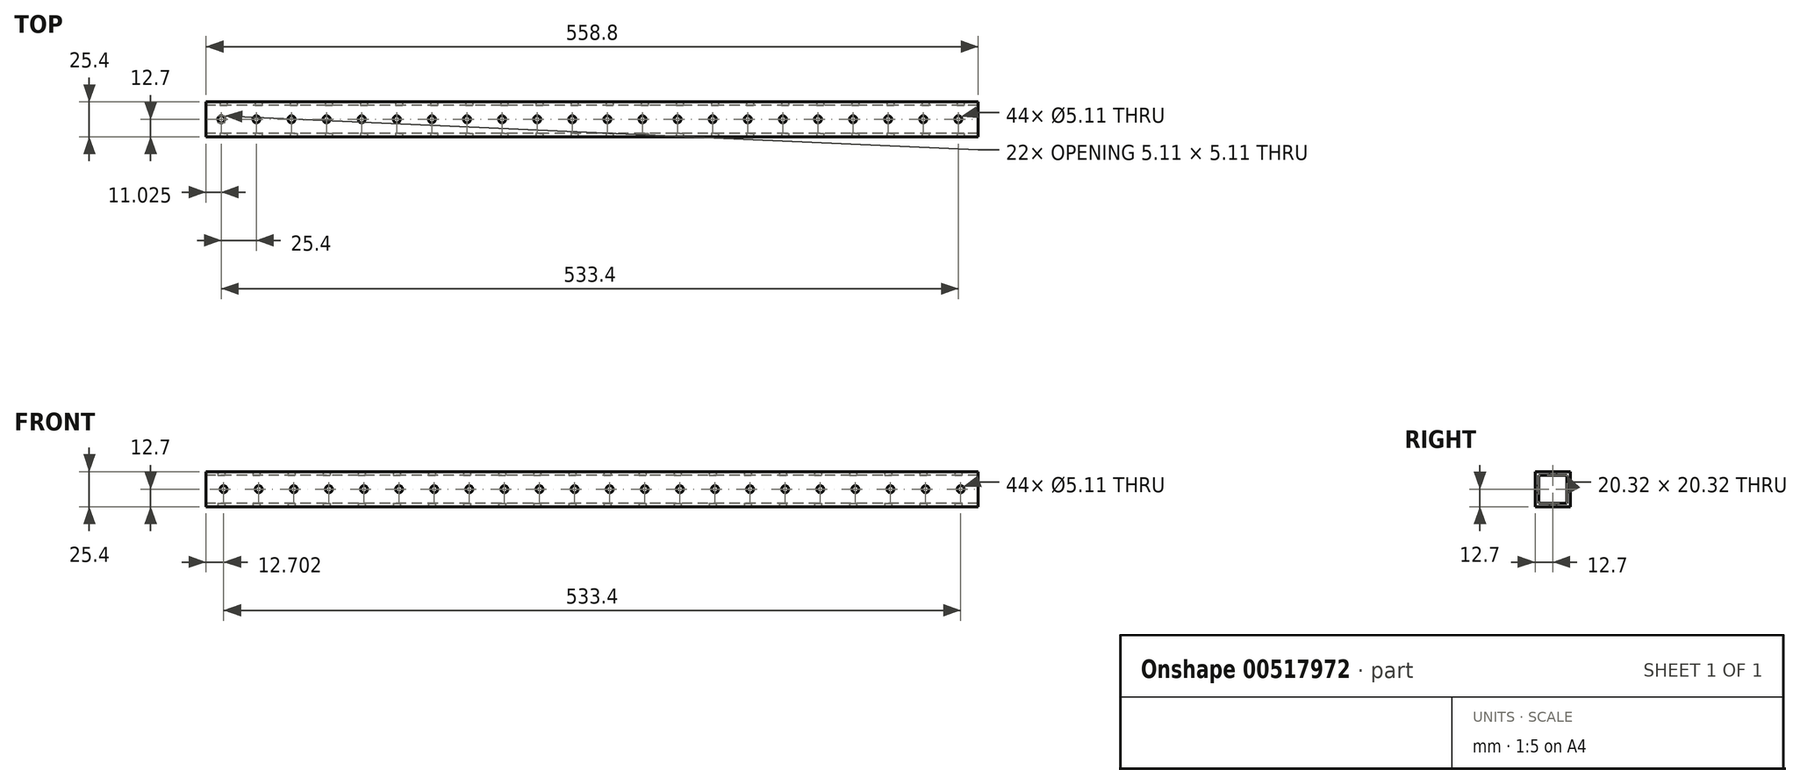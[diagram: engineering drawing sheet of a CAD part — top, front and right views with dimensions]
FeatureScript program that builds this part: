
annotation { "Feature Type Name" : "Feature", "Feature Type Description" : "" }
export const myFeature = defineFeature(function(context is Context, id is Id, definition is map)
    precondition{}
    {
        {
            var Q0;
            Q0=qCreatedBy(makeId("Top.planeOp"),FACE);
            var sketch = newSketch(context, id + "F0", { "sketchPlane" : qUnion([Q0])});
            skLineSegment(sketch, "E0.bottom", {"start": v(-249.34, 12.7) * mm, "end": v(309.46, 12.7) * mm});
            skLineSegment(sketch, "E0.top", {"start": v(-249.34, -12.7) * mm, "end": v(309.46, -12.7) * mm});
            skLineSegment(sketch, "E0.left", {"start": v(-249.34, 12.7) * mm, "end": v(-249.34, -12.7) * mm});
            skLineSegment(sketch, "E0.right", {"start": v(309.46, 12.7) * mm, "end": v(309.46, -12.7) * mm});
            skCircle(sketch, "E1", {"center": v(295.09, 0) * mm, "radius": 2.55 * mm});
            skCircle(sketch, "E2.1.0.0", {"center": v(269.69, 0) * mm, "radius": 2.55 * mm});
            skCircle(sketch, "E2.2.0.0", {"center": v(244.29, 0) * mm, "radius": 2.55 * mm});
            skCircle(sketch, "E2.3.0.0", {"center": v(218.89, 0) * mm, "radius": 2.55 * mm});
            skCircle(sketch, "E2.4.0.0", {"center": v(193.49, 0) * mm, "radius": 2.55 * mm});
            skCircle(sketch, "E2.5.0.0", {"center": v(168.09, 0) * mm, "radius": 2.55 * mm});
            skCircle(sketch, "E2.6.0.0", {"center": v(142.69, 0) * mm, "radius": 2.55 * mm});
            skCircle(sketch, "E2.7.0.0", {"center": v(117.29, 0) * mm, "radius": 2.55 * mm});
            skCircle(sketch, "E2.8.0.0", {"center": v(91.89, 0) * mm, "radius": 2.55 * mm});
            skCircle(sketch, "E2.9.0.0", {"center": v(66.49, 0) * mm, "radius": 2.55 * mm});
            skCircle(sketch, "E2.10.0.0", {"center": v(41.09, 0) * mm, "radius": 2.55 * mm});
            skCircle(sketch, "E2.11.0.0", {"center": v(15.69, 0) * mm, "radius": 2.55 * mm});
            skCircle(sketch, "E2.12.0.0", {"center": v(-9.71, 0) * mm, "radius": 2.55 * mm});
            skCircle(sketch, "E2.13.0.0", {"center": v(-35.11, 0) * mm, "radius": 2.55 * mm});
            skCircle(sketch, "E2.14.0.0", {"center": v(-60.51, 0) * mm, "radius": 2.55 * mm});
            skCircle(sketch, "E2.15.0.0", {"center": v(-85.91, 0) * mm, "radius": 2.55 * mm});
            skCircle(sketch, "E2.16.0.0", {"center": v(-111.31, 0) * mm, "radius": 2.55 * mm});
            skCircle(sketch, "E2.17.0.0", {"center": v(-136.71, 0) * mm, "radius": 2.55 * mm});
            skCircle(sketch, "E2.18.0.0", {"center": v(-162.11, 0) * mm, "radius": 2.55 * mm});
            skCircle(sketch, "E2.19.0.0", {"center": v(-187.51, 0) * mm, "radius": 2.55 * mm});
            skLineSegment(sketch, "E2.direction1", {"start": v(295.09, 0) * mm, "end": v(269.69, 0) * mm, "construction": true});
            skCircle(sketch, "E3.0.20.0", {"center": v(-212.91, 0) * mm, "radius": 2.55 * mm});
            skCircle(sketch, "E3.0.21.0", {"center": v(-238.31, 0) * mm, "radius": 2.55 * mm});
            skSolve(sketch);
        }
        {
            var Q0;
            Q0 = qSketchRegion(id + "F0", true);
            extrude(context, id + "F1", {"entities" : qUnion([Q0]), "depth" : 25.4 * mm, "offsetDistance" : 25.4 * mm});
        }
        {
            var Q0;
            Q0=makeQuery(id+"F1.opExtrude","SWEPT_FACE",FACE,{"disambiguationData":[OSD([sQuery(id+"F0.wireOp",EDGE,"E0.left")])]});
            var sketch = newSketch(context, id + "F2", { "sketchPlane" : qUnion([Q0])});
            skLineSegment(sketch, "E4.bottom", {"start": v(-10.16, 22.86) * mm, "end": v(10.16, 22.86) * mm});
            skLineSegment(sketch, "E4.top", {"start": v(-10.16, 2.54) * mm, "end": v(10.16, 2.54) * mm});
            skLineSegment(sketch, "E4.left", {"start": v(-10.16, 22.86) * mm, "end": v(-10.16, 2.54) * mm});
            skLineSegment(sketch, "E4.right", {"start": v(10.16, 22.86) * mm, "end": v(10.16, 2.54) * mm});
            skSolve(sketch);
        }
        {
            var Q0;
            Q0=makeQuery(id+"F2.imprint","IMPRINT",FACE,{"disambiguationData":[TD([[makeQuery(id+"F2.imprint","IMPRINT",EDGE,{"derivedFrom":sQuery(id+"F2.wireOp",EDGE,"E4.bottom")}),-1.0]])]});
            extrude(context, id + "F3", {"entities" : qUnion([Q0]), "operationType" : NewBodyOperationType.REMOVE, "oppositeDirection" : true, "depth" : 508 * mm, "offsetDistance" : 25.4 * mm});
        }
        {
            var Q0;
            Q0=makeQuery(id+"F1.opExtrude","SWEPT_FACE",FACE,{"disambiguationData":[OSD([sQuery(id+"F0.wireOp",EDGE,"E0.top")])]});
            var sketch = newSketch(context, id + "F4", { "sketchPlane" : qUnion([Q0])});
            skCircle(sketch, "E5", {"center": v(-236.64, 12.7) * mm, "radius": 2.55 * mm});
            skCircle(sketch, "E6.1.0.0", {"center": v(-211.24, 12.7) * mm, "radius": 2.55 * mm});
            skCircle(sketch, "E6.2.0.0", {"center": v(-185.84, 12.7) * mm, "radius": 2.55 * mm});
            skCircle(sketch, "E6.3.0.0", {"center": v(-160.44, 12.7) * mm, "radius": 2.55 * mm});
            skCircle(sketch, "E6.4.0.0", {"center": v(-135.04, 12.7) * mm, "radius": 2.55 * mm});
            skCircle(sketch, "E6.5.0.0", {"center": v(-109.64, 12.7) * mm, "radius": 2.55 * mm});
            skCircle(sketch, "E6.6.0.0", {"center": v(-84.24, 12.7) * mm, "radius": 2.55 * mm});
            skCircle(sketch, "E6.7.0.0", {"center": v(-58.84, 12.7) * mm, "radius": 2.55 * mm});
            skCircle(sketch, "E6.8.0.0", {"center": v(-33.44, 12.7) * mm, "radius": 2.55 * mm});
            skCircle(sketch, "E6.9.0.0", {"center": v(-8.04, 12.7) * mm, "radius": 2.55 * mm});
            skCircle(sketch, "E6.10.0.0", {"center": v(17.36, 12.7) * mm, "radius": 2.55 * mm});
            skCircle(sketch, "E6.11.0.0", {"center": v(42.76, 12.7) * mm, "radius": 2.55 * mm});
            skCircle(sketch, "E6.12.0.0", {"center": v(68.16, 12.7) * mm, "radius": 2.55 * mm});
            skCircle(sketch, "E6.13.0.0", {"center": v(93.56, 12.7) * mm, "radius": 2.55 * mm});
            skCircle(sketch, "E6.14.0.0", {"center": v(118.96, 12.7) * mm, "radius": 2.55 * mm});
            skCircle(sketch, "E6.15.0.0", {"center": v(144.36, 12.7) * mm, "radius": 2.55 * mm});
            skCircle(sketch, "E6.16.0.0", {"center": v(169.76, 12.7) * mm, "radius": 2.55 * mm});
            skCircle(sketch, "E6.17.0.0", {"center": v(195.16, 12.7) * mm, "radius": 2.55 * mm});
            skCircle(sketch, "E6.18.0.0", {"center": v(220.56, 12.7) * mm, "radius": 2.55 * mm});
            skCircle(sketch, "E6.19.0.0", {"center": v(245.96, 12.7) * mm, "radius": 2.55 * mm});
            skCircle(sketch, "E6.20.0.0", {"center": v(271.36, 12.7) * mm, "radius": 2.55 * mm});
            skCircle(sketch, "E6.21.0.0", {"center": v(296.76, 12.7) * mm, "radius": 2.55 * mm});
            skLineSegment(sketch, "E6.direction1", {"start": v(-236.64, 12.7) * mm, "end": v(-211.24, 12.7) * mm, "construction": true});
            skSolve(sketch);
        }
        {
            var Q0;
            Q0=sQuery(id+"F4.wireOp",VERTEX,"E6.14.0.0.center");
            var Q1;
            Q1=sQuery(id+"F4.wireOp",VERTEX,"E6.18.0.0.center");
            var Q2;
            Q2=sQuery(id+"F4.wireOp",VERTEX,"E6.11.0.0.center");
            var Q3;
            Q3=sQuery(id+"F4.wireOp",VERTEX,"E6.16.0.0.center");
            var Q4;
            Q4=sQuery(id+"F4.wireOp",VERTEX,"E6.20.0.0.center");
            var Q5;
            Q5=sQuery(id+"F4.wireOp",VERTEX,"E6.8.0.0.center");
            var Q6;
            Q6=sQuery(id+"F4.wireOp",VERTEX,"E6.17.0.0.center");
            var Q7;
            Q7=sQuery(id+"F4.wireOp",VERTEX,"E6.19.0.0.center");
            var Q8;
            Q8=sQuery(id+"F4.wireOp",VERTEX,"E6.7.0.0.center");
            var Q9;
            Q9=sQuery(id+"F4.wireOp",VERTEX,"E6.6.0.0.center");
            var Q10;
            Q10=sQuery(id+"F4.wireOp",VERTEX,"E6.2.0.0.center");
            var Q11;
            Q11=sQuery(id+"F4.wireOp",VERTEX,"E5.center");
            var Q12;
            Q12=sQuery(id+"F4.wireOp",VERTEX,"E6.10.0.0.center");
            var Q13;
            Q13=sQuery(id+"F4.wireOp",VERTEX,"E6.9.0.0.center");
            var Q14;
            Q14=sQuery(id+"F4.wireOp",VERTEX,"E6.21.0.0.center");
            var Q15;
            Q15=sQuery(id+"F4.wireOp",VERTEX,"E6.12.0.0.center");
            var Q16;
            Q16=sQuery(id+"F4.wireOp",VERTEX,"E6.13.0.0.center");
            var Q17;
            Q17=sQuery(id+"F4.wireOp",VERTEX,"E6.15.0.0.center");
            var Q18;
            Q18=sQuery(id+"F4.wireOp",VERTEX,"E6.1.0.0.center");
            var Q19;
            Q19=sQuery(id+"F4.wireOp",VERTEX,"E6.5.0.0.center");
            var Q20;
            Q20=sQuery(id+"F4.wireOp",VERTEX,"E6.4.0.0.center");
            var Q21;
            Q21=sQuery(id+"F4.wireOp",VERTEX,"E6.3.0.0.center");
            var Q22;
            Q22=makeQuery(id+"F1.opExtrude","SWEPT_BODY",BODY,{"disambiguationData":[OSD([sQuery(id+"F0.wireOp",EDGE,"E0.bottom"),sQuery(id+"F0.wireOp",EDGE,"E0.top"),sQuery(id+"F0.wireOp",EDGE,"E0.left"),sQuery(id+"F0.wireOp",EDGE,"E0.right"),sQuery(id+"F0.wireOp",EDGE,"E1"),sQuery(id+"F0.wireOp",EDGE,"E2.1.0.0"),sQuery(id+"F0.wireOp",EDGE,"E2.2.0.0"),sQuery(id+"F0.wireOp",EDGE,"E2.3.0.0"),sQuery(id+"F0.wireOp",EDGE,"E2.4.0.0"),sQuery(id+"F0.wireOp",EDGE,"E2.5.0.0"),sQuery(id+"F0.wireOp",EDGE,"E2.6.0.0"),sQuery(id+"F0.wireOp",EDGE,"E2.7.0.0"),sQuery(id+"F0.wireOp",EDGE,"E2.8.0.0"),sQuery(id+"F0.wireOp",EDGE,"E2.9.0.0"),sQuery(id+"F0.wireOp",EDGE,"E2.10.0.0"),sQuery(id+"F0.wireOp",EDGE,"E2.11.0.0"),sQuery(id+"F0.wireOp",EDGE,"E2.12.0.0"),sQuery(id+"F0.wireOp",EDGE,"E2.13.0.0"),sQuery(id+"F0.wireOp",EDGE,"E2.14.0.0"),sQuery(id+"F0.wireOp",EDGE,"E2.15.0.0"),sQuery(id+"F0.wireOp",EDGE,"E2.16.0.0"),sQuery(id+"F0.wireOp",EDGE,"E2.17.0.0"),sQuery(id+"F0.wireOp",EDGE,"E2.18.0.0"),sQuery(id+"F0.wireOp",EDGE,"E2.19.0.0"),sQuery(id+"F0.wireOp",EDGE,"E3.0.20.0"),sQuery(id+"F0.wireOp",EDGE,"E3.0.21.0")])]});
            hole(context, id + "F5", {"style" : HoleStyle.SIMPLE, "endStyle" : HoleEndStyle.THROUGH, "holeDiameter" : 5.1 * mm, "isTappedThrough" : true, "tappedDepth" : 12.7 * mm, "tapClearance" : 3, "locations" : qUnion([Q0, Q1, Q2, Q3, Q4, Q5, Q6, Q7, Q8, Q9, Q10, Q11, Q12, Q13, Q14, Q15, Q16, Q17, Q18, Q19, Q20, Q21]), "scope" : qUnion([Q22])});
        }
        {
            var Q0;
            Q0=makeQuery(id+"F1.opExtrude","SWEPT_FACE",FACE,{"disambiguationData":[OSD([sQuery(id+"F0.wireOp",EDGE,"E0.right")])]});
            var sketch = newSketch(context, id + "F6", { "sketchPlane" : qUnion([Q0])});
            skLineSegment(sketch, "E7.bottom", {"start": v(-10.16, 22.86) * mm, "end": v(10.16, 22.86) * mm});
            skLineSegment(sketch, "E7.top", {"start": v(-10.16, 2.54) * mm, "end": v(10.16, 2.54) * mm});
            skLineSegment(sketch, "E7.left", {"start": v(-10.16, 22.86) * mm, "end": v(-10.16, 2.54) * mm});
            skLineSegment(sketch, "E7.right", {"start": v(10.16, 22.86) * mm, "end": v(10.16, 2.54) * mm});
            skSolve(sketch);
        }
        {
            var Q0;
            Q0=makeQuery(id+"F6.imprint","IMPRINT",FACE,{"disambiguationData":[TD([[makeQuery(id+"F6.imprint","IMPRINT",EDGE,{"derivedFrom":sQuery(id+"F6.wireOp",EDGE,"E7.bottom")}),-1.0]])]});
            extrude(context, id + "F7", {"entities" : qUnion([Q0]), "operationType" : NewBodyOperationType.REMOVE, "oppositeDirection" : true, "depth" : 558.8 * mm, "offsetDistance" : 25.4 * mm});
        }
    });
